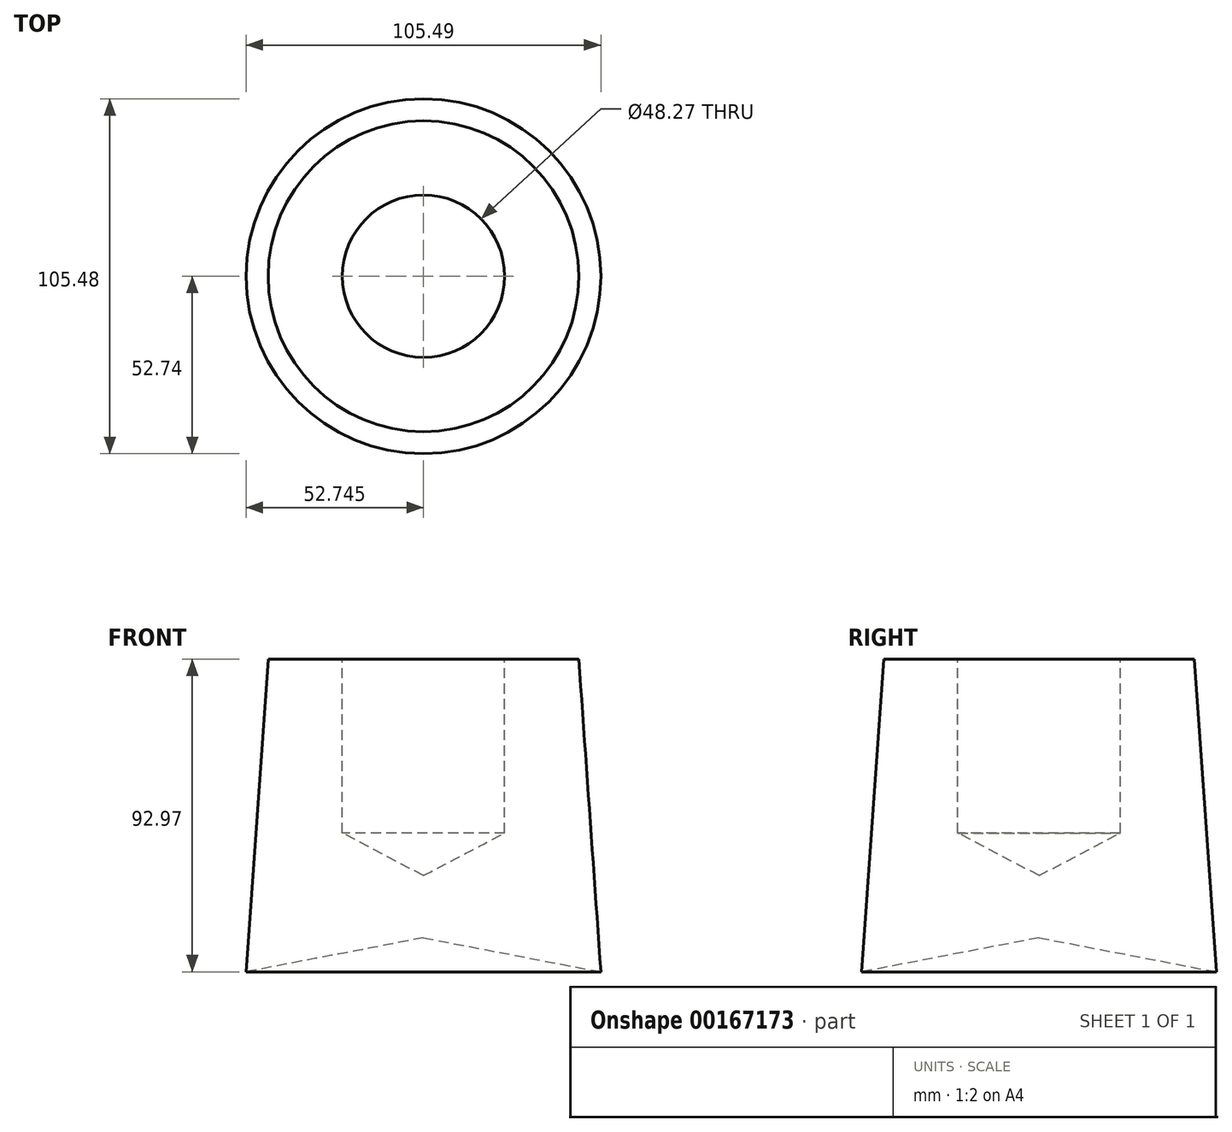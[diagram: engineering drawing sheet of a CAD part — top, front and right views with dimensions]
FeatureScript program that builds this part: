
annotation { "Feature Type Name" : "Feature", "Feature Type Description" : "" }
export const myFeature = defineFeature(function(context is Context, id is Id, definition is map)
    precondition{}
    {
        {
            var Q0;
            Q0=qCreatedBy(makeId("Front.planeOp"),FACE);
            var sketch = newSketch(context, id + "F0", { "sketchPlane" : qUnion([Q0])});
            skLineSegment(sketch, "E0", {"start": v(-57.36, 51.7) * mm, "end": v(-35.31, 51.7) * mm});
            skLineSegment(sketch, "E1", {"start": v(-35.31, 51.7) * mm, "end": v(-35.31, 0) * mm});
            skLineSegment(sketch, "E2", {"start": v(-35.31, 0) * mm, "end": v(-11.17, -12.66) * mm});
            skLineSegment(sketch, "E3", {"start": v(-11.17, -12.66) * mm, "end": v(-11.17, -31.14) * mm});
            skLineSegment(sketch, "E4", {"start": v(-57.36, 51.7) * mm, "end": v(-63.92, -41.27) * mm});
            skLineSegment(sketch, "E5", {"start": v(-63.92, -41.27) * mm, "end": v(-11.17, -31.14) * mm});
            skSolve(sketch);
        }
        {
            var Q0;
            Q0=makeQuery(id+"F0.imprint","IMPRINT",FACE,{"disambiguationData":[TD([[makeQuery(id+"F0.imprint","IMPRINT",EDGE,{"derivedFrom":sQuery(id+"F0.wireOp",EDGE,"E0")}),-1.0]])]});
            var Q1;
            Q1=sQuery(id+"F0.wireOp",EDGE,"E3");
            revolve(context, id + "F1", {"entities" : qUnion([Q0]), "axis" : qUnion([Q1]), "revolveType" : RevolveType.FULL});
        }
    });
